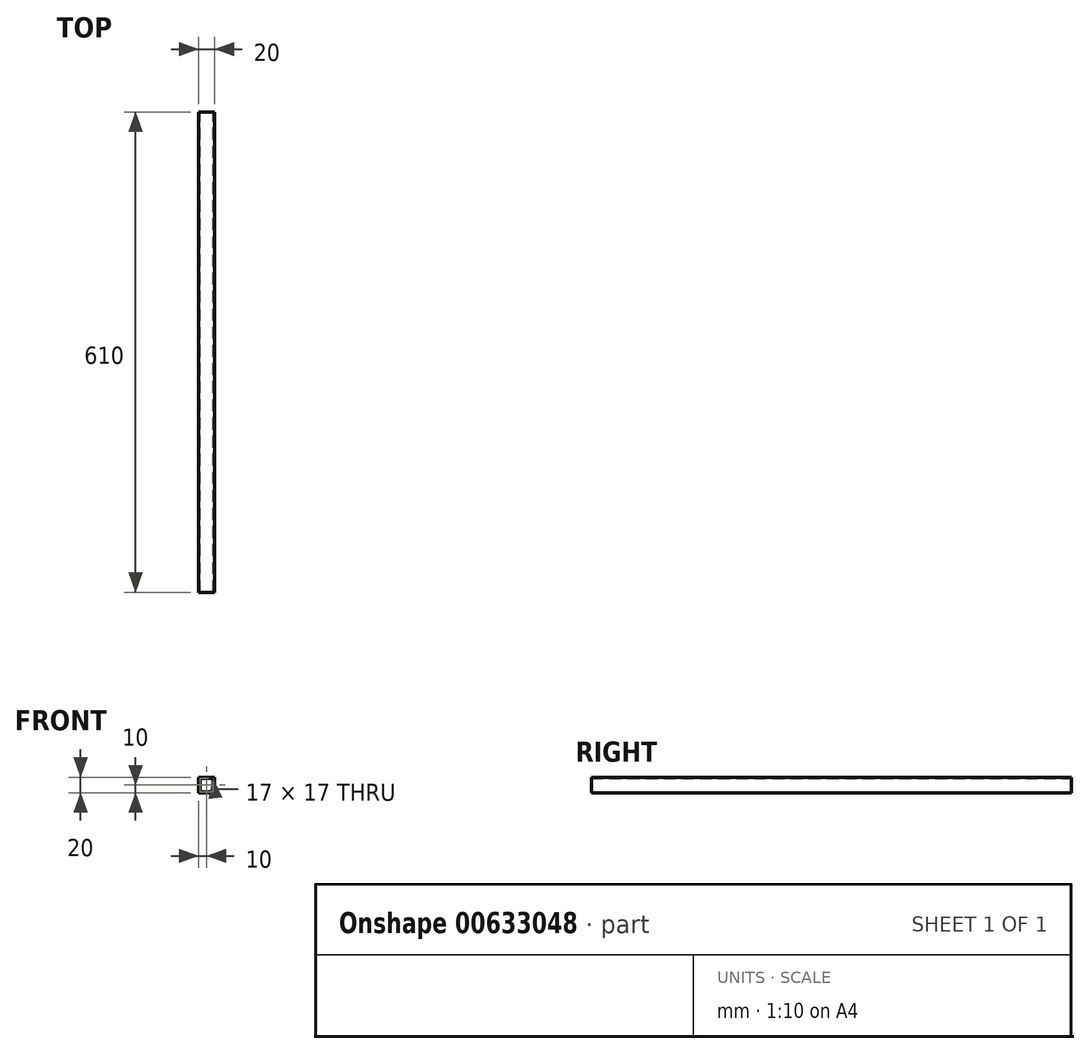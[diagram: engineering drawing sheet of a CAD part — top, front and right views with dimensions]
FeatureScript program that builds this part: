
annotation { "Feature Type Name" : "Feature", "Feature Type Description" : "" }
export const myFeature = defineFeature(function(context is Context, id is Id, definition is map)
    precondition{}
    {
        {
            var Q0;
            Q0=qCreatedBy(makeId("Front.planeOp"),FACE);
            var sketch = newSketch(context, id + "F0", { "sketchPlane" : qUnion([Q0])});
            skLineSegment(sketch, "E0.bottom", {"start": v(0, 0) * mm, "end": v(20, 0) * mm});
            skLineSegment(sketch, "E0.top", {"start": v(0, -20) * mm, "end": v(20, -20) * mm});
            skLineSegment(sketch, "E0.left", {"start": v(0, 0) * mm, "end": v(0, -20) * mm});
            skLineSegment(sketch, "E0.right", {"start": v(20, 0) * mm, "end": v(20, -20) * mm});
            skLineSegment(sketch, "E1.0", {"start": v(1.5, -1.5) * mm, "end": v(18.5, -1.5) * mm});
            skLineSegment(sketch, "E1.1", {"start": v(1.5, -1.5) * mm, "end": v(1.5, -18.5) * mm});
            skLineSegment(sketch, "E1.2", {"start": v(1.5, -18.5) * mm, "end": v(18.5, -18.5) * mm});
            skLineSegment(sketch, "E1.3", {"start": v(18.5, -1.5) * mm, "end": v(18.5, -18.5) * mm});
            skSolve(sketch);
        }
        {
            var Q0;
            Q0=makeQuery(id+"F0.imprint","IMPRINT",FACE,{"disambiguationData":[TD([[makeQuery(id+"F0.imprint","IMPRINT",EDGE,{"derivedFrom":sQuery(id+"F0.wireOp",EDGE,"E0.bottom")}),-1.0]])]});
            extrude(context, id + "F1", {"entities" : qUnion([Q0]), "depth" : 650 * mm - 40 * mm, "offsetDistance" : 25 * mm});
        }
    });
